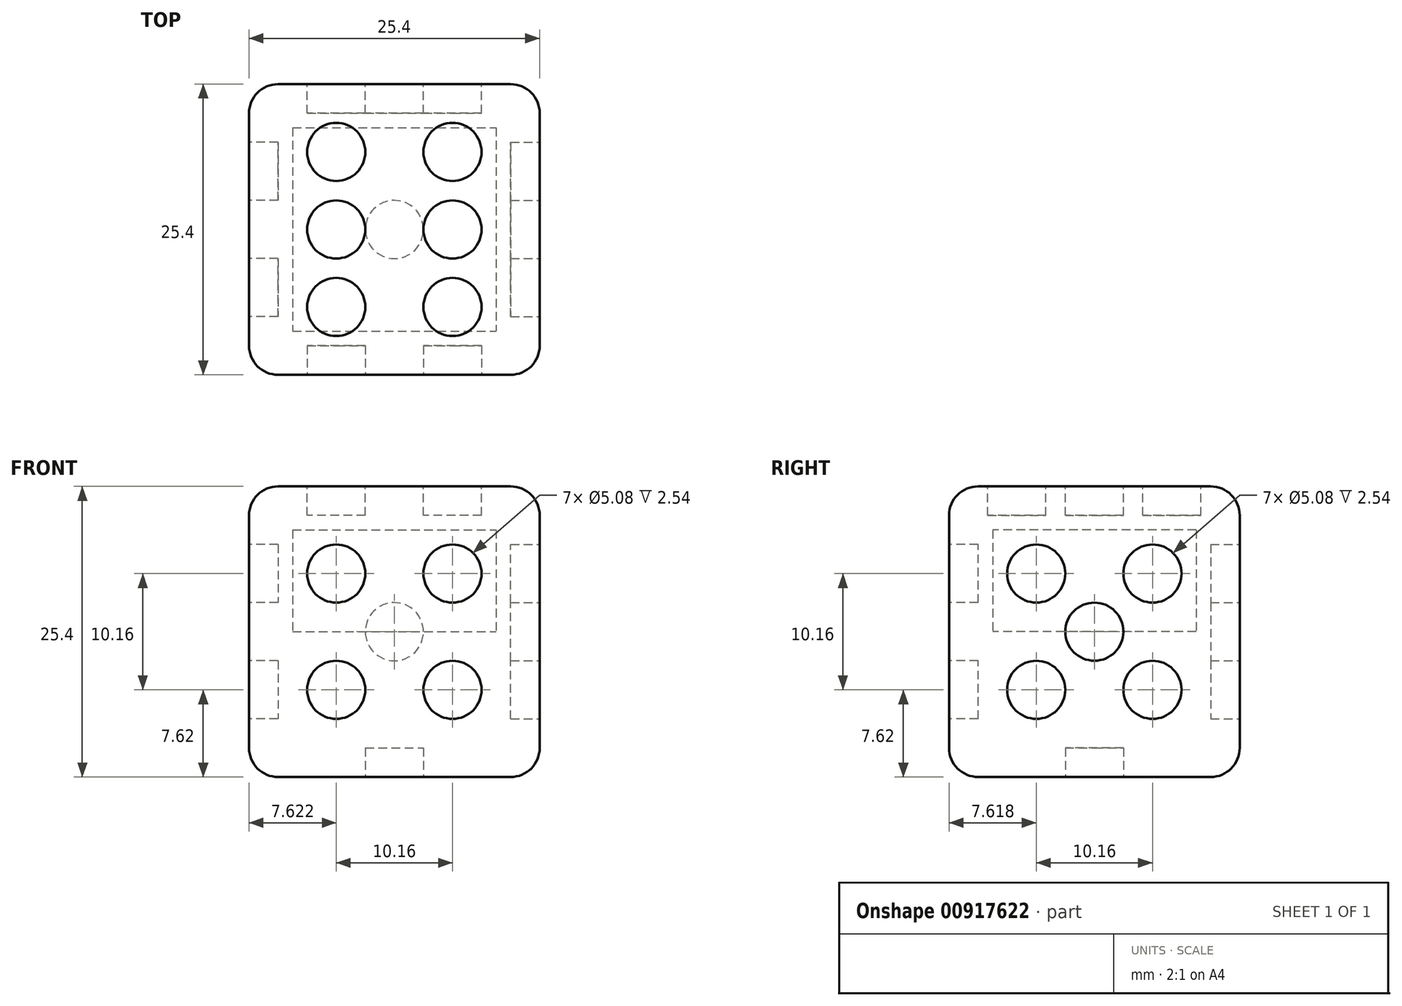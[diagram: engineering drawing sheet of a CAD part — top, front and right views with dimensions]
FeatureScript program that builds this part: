
annotation { "Feature Type Name" : "Feature", "Feature Type Description" : "" }
export const myFeature = defineFeature(function(context is Context, id is Id, definition is map)
    precondition{}
    {
        {
            var Q0;
            Q0=qCreatedBy(makeId("Top.planeOp"),FACE);
            var sketch = newSketch(context, id + "F0", { "sketchPlane" : qUnion([Q0])});
            skLineSegment(sketch, "E0.bottom", {"start": v(-52.85, 44.08) * mm, "end": v(-27.45, 44.08) * mm});
            skLineSegment(sketch, "E0.top", {"start": v(-52.85, 18.68) * mm, "end": v(-27.45, 18.68) * mm});
            skLineSegment(sketch, "E0.left", {"start": v(-52.85, 44.08) * mm, "end": v(-52.85, 18.68) * mm});
            skLineSegment(sketch, "E0.right", {"start": v(-27.45, 44.08) * mm, "end": v(-27.45, 18.68) * mm});
            skSolve(sketch);
        }
        {
            var Q0;
            Q0=makeQuery(id+"F0.imprint","IMPRINT",FACE,{"disambiguationData":[TD([[makeQuery(id+"F0.imprint","IMPRINT",EDGE,{"derivedFrom":sQuery(id+"F0.wireOp",EDGE,"E0.bottom")}),-1.0]])]});
            extrude(context, id + "F1", {"entities" : qUnion([Q0]), "depth" : 12.7 * mm, "offsetDistance" : 25.4 * mm});
        }
        {
            var Q0;
            Q0=makeQuery(id+"F1.opExtrude","CAP_FACE",FACE,{"disambiguationData":[OSD([sQuery(id+"F0.wireOp",EDGE,"E0.bottom"),sQuery(id+"F0.wireOp",EDGE,"E0.top"),sQuery(id+"F0.wireOp",EDGE,"E0.left"),sQuery(id+"F0.wireOp",EDGE,"E0.right")])],"isStart":false});
            var sketch = newSketch(context, id + "F2", { "sketchPlane" : qUnion([Q0])});
            skLineSegment(sketch, "E1.bottom", {"start": v(-49.04, 40.27) * mm, "end": v(-31.26, 40.27) * mm});
            skLineSegment(sketch, "E1.top", {"start": v(-49.04, 22.49) * mm, "end": v(-31.26, 22.49) * mm});
            skLineSegment(sketch, "E1.left", {"start": v(-49.04, 40.27) * mm, "end": v(-49.04, 22.49) * mm});
            skLineSegment(sketch, "E1.right", {"start": v(-31.26, 40.27) * mm, "end": v(-31.26, 22.49) * mm});
            skLineSegment(sketch, "E2.bottom", {"start": v(-52.85, 44.08) * mm, "end": v(-27.45, 44.08) * mm});
            skLineSegment(sketch, "E2.top", {"start": v(-52.85, 18.68) * mm, "end": v(-27.45, 18.68) * mm});
            skLineSegment(sketch, "E2.left", {"start": v(-52.85, 44.08) * mm, "end": v(-52.85, 18.68) * mm});
            skLineSegment(sketch, "E2.right", {"start": v(-27.45, 44.08) * mm, "end": v(-27.45, 18.68) * mm});
            skSolve(sketch);
        }
        {
            var Q0;
            Q0=makeQuery(id+"F2.imprint","IMPRINT",FACE,{"disambiguationData":[TD([[makeQuery(id+"F2.imprint","IMPRINT",EDGE,{"derivedFrom":sQuery(id+"F2.wireOp",EDGE,"E1.bottom")}),1.0]])]});
            extrude(context, id + "F3", {"entities" : qUnion([Q0]), "operationType" : NewBodyOperationType.ADD, "depth" : 8.9 * mm, "offsetDistance" : 25.4 * mm});
        }
        {
            var Q0;
            Q0=makeQuery(id+"F3.opExtrude","CAP_FACE",FACE,{"disambiguationData":[OSD([sQuery(id+"F2.wireOp",EDGE,"E1.bottom"),sQuery(id+"F2.wireOp",EDGE,"E1.top"),sQuery(id+"F2.wireOp",EDGE,"E1.left"),sQuery(id+"F2.wireOp",EDGE,"E1.right"),sQuery(id+"F2.wireOp",EDGE,"E2.bottom"),sQuery(id+"F2.wireOp",EDGE,"E2.top"),sQuery(id+"F2.wireOp",EDGE,"E2.left"),sQuery(id+"F2.wireOp",EDGE,"E2.right")])],"isStart":false});
            var sketch = newSketch(context, id + "F4", { "sketchPlane" : qUnion([Q0])});
            skLineSegment(sketch, "E3.bottom", {"start": v(-52.85, 44.08) * mm, "end": v(-27.45, 44.08) * mm});
            skLineSegment(sketch, "E3.top", {"start": v(-52.85, 18.68) * mm, "end": v(-27.45, 18.68) * mm});
            skLineSegment(sketch, "E3.left", {"start": v(-52.85, 44.08) * mm, "end": v(-52.85, 18.68) * mm});
            skLineSegment(sketch, "E3.right", {"start": v(-27.45, 44.08) * mm, "end": v(-27.45, 18.68) * mm});
            skSolve(sketch);
        }
        {
            var Q0;
            Q0 = qSketchRegion(id + "F4", true);
            extrude(context, id + "F5", {"entities" : qUnion([Q0]), "operationType" : NewBodyOperationType.ADD, "depth" : 3.8 * mm, "offsetDistance" : 25.4 * mm});
        }
        {
            var Q0;
            Q0=makeQuery(id+"F5.opExtrude","CAP_EDGE",EDGE,{"disambiguationData":[OSD([sQuery(id+"F4.wireOp",EDGE,"E3.top")])],"isStart":false});
            var Q1;
            Q1=makeQuery(id+"F5.opExtrude","CAP_EDGE",EDGE,{"disambiguationData":[OSD([sQuery(id+"F4.wireOp",EDGE,"E3.right")])],"isStart":false});
            var Q2;
            Q2=makeQuery(id+"F5.boolean.opBoolean","MERGE",EDGE,{"derivedFrom":[makeQuery(id+"F3.boolean.opBoolean","MERGE",EDGE,{"derivedFrom":[makeQuery(id+"F1.opExtrude","SWEPT_EDGE",EDGE,{"disambiguationData":[OSD([sQuery(id+"F0.wireOp",EDGE,"E0.top"),sQuery(id+"F0.wireOp",EDGE,"E0.right")])]}),makeQuery(id+"F3.opExtrude","SWEPT_EDGE",EDGE,{"disambiguationData":[OSD([sQuery(id+"F2.wireOp",EDGE,"E2.top"),sQuery(id+"F2.wireOp",EDGE,"E2.right")])]})]}),makeQuery(id+"F5.opExtrude","SWEPT_EDGE",EDGE,{"disambiguationData":[OSD([sQuery(id+"F4.wireOp",EDGE,"E3.top"),sQuery(id+"F4.wireOp",EDGE,"E3.right")])]})]});
            var Q3;
            Q3=makeQuery(id+"F5.boolean.opBoolean","MERGE",EDGE,{"derivedFrom":[makeQuery(id+"F3.boolean.opBoolean","MERGE",EDGE,{"derivedFrom":[makeQuery(id+"F1.opExtrude","SWEPT_EDGE",EDGE,{"disambiguationData":[OSD([sQuery(id+"F0.wireOp",EDGE,"E0.bottom"),sQuery(id+"F0.wireOp",EDGE,"E0.right")])]}),makeQuery(id+"F3.opExtrude","SWEPT_EDGE",EDGE,{"disambiguationData":[OSD([sQuery(id+"F2.wireOp",EDGE,"E2.bottom"),sQuery(id+"F2.wireOp",EDGE,"E2.right")])]})]}),makeQuery(id+"F5.opExtrude","SWEPT_EDGE",EDGE,{"disambiguationData":[OSD([sQuery(id+"F4.wireOp",EDGE,"E3.bottom"),sQuery(id+"F4.wireOp",EDGE,"E3.right")])]})]});
            var Q4;
            Q4=makeQuery(id+"F5.opExtrude","CAP_EDGE",EDGE,{"disambiguationData":[OSD([sQuery(id+"F4.wireOp",EDGE,"E3.bottom")])],"isStart":false});
            var Q5;
            Q5=makeQuery(id+"F5.opExtrude","CAP_EDGE",EDGE,{"disambiguationData":[OSD([sQuery(id+"F4.wireOp",EDGE,"E3.left")])],"isStart":false});
            var Q6;
            Q6=makeQuery(id+"F5.boolean.opBoolean","MERGE",EDGE,{"derivedFrom":[makeQuery(id+"F3.boolean.opBoolean","MERGE",EDGE,{"derivedFrom":[makeQuery(id+"F1.opExtrude","SWEPT_EDGE",EDGE,{"disambiguationData":[OSD([sQuery(id+"F0.wireOp",EDGE,"E0.top"),sQuery(id+"F0.wireOp",EDGE,"E0.left")])]}),makeQuery(id+"F3.opExtrude","SWEPT_EDGE",EDGE,{"disambiguationData":[OSD([sQuery(id+"F2.wireOp",EDGE,"E2.top"),sQuery(id+"F2.wireOp",EDGE,"E2.left")])]})]}),makeQuery(id+"F5.opExtrude","SWEPT_EDGE",EDGE,{"disambiguationData":[OSD([sQuery(id+"F4.wireOp",EDGE,"E3.top"),sQuery(id+"F4.wireOp",EDGE,"E3.left")])]})]});
            var Q7;
            Q7=makeQuery(id+"F1.opExtrude","CAP_EDGE",EDGE,{"disambiguationData":[OSD([sQuery(id+"F0.wireOp",EDGE,"E0.top")])],"isStart":true});
            var Q8;
            Q8=makeQuery(id+"F1.opExtrude","CAP_EDGE",EDGE,{"disambiguationData":[OSD([sQuery(id+"F0.wireOp",EDGE,"E0.left")])],"isStart":true});
            var Q9;
            Q9=makeQuery(id+"F1.opExtrude","CAP_EDGE",EDGE,{"disambiguationData":[OSD([sQuery(id+"F0.wireOp",EDGE,"E0.bottom")])],"isStart":true});
            var Q10;
            Q10=makeQuery(id+"F1.opExtrude","CAP_EDGE",EDGE,{"disambiguationData":[OSD([sQuery(id+"F0.wireOp",EDGE,"E0.right")])],"isStart":true});
            var Q11;
            Q11=makeQuery(id+"F5.boolean.opBoolean","MERGE",EDGE,{"derivedFrom":[makeQuery(id+"F3.boolean.opBoolean","MERGE",EDGE,{"derivedFrom":[makeQuery(id+"F1.opExtrude","SWEPT_EDGE",EDGE,{"disambiguationData":[OSD([sQuery(id+"F0.wireOp",EDGE,"E0.bottom"),sQuery(id+"F0.wireOp",EDGE,"E0.left")])]}),makeQuery(id+"F3.opExtrude","SWEPT_EDGE",EDGE,{"disambiguationData":[OSD([sQuery(id+"F2.wireOp",EDGE,"E2.bottom"),sQuery(id+"F2.wireOp",EDGE,"E2.left")])]})]}),makeQuery(id+"F5.opExtrude","SWEPT_EDGE",EDGE,{"disambiguationData":[OSD([sQuery(id+"F4.wireOp",EDGE,"E3.bottom"),sQuery(id+"F4.wireOp",EDGE,"E3.left")])]})]});
            fillet(context, id + "F6", {"entities" : qUnion([Q0, Q1, Q2, Q3, Q4, Q5, Q6, Q7, Q8, Q9, Q10, Q11]), "radius" : 2.54 * mm, "tangentPropagation" : true, "allowEdgeOverflow" : false});
        }
        {
            var Q0;
            Q0=makeQuery(id+"F5.opExtrude","CAP_FACE",FACE,{"disambiguationData":[OSD([sQuery(id+"F4.wireOp",EDGE,"E3.bottom"),sQuery(id+"F4.wireOp",EDGE,"E3.top"),sQuery(id+"F4.wireOp",EDGE,"E3.left"),sQuery(id+"F4.wireOp",EDGE,"E3.right")])],"isStart":false});
            var sketch = newSketch(context, id + "F7", { "sketchPlane" : qUnion([Q0])});
            skLineSegment(sketch, "E4", {"start": v(-50.3, 41.54) * mm, "end": v(-45.23, 41.54) * mm});
            skLineSegment(sketch, "E5", {"start": v(-29.99, 41.54) * mm, "end": v(-29.99, 38.15) * mm});
            skLineSegment(sketch, "E6", {"start": v(-29.99, 21.22) * mm, "end": v(-35.07, 21.22) * mm});
            skLineSegment(sketch, "E7", {"start": v(-50.3, 21.22) * mm, "end": v(-50.3, 24.6) * mm});
            skLineSegment(sketch, "E8", {"start": v(-50.3, 24.6) * mm, "end": v(-45.23, 24.6) * mm});
            skLineSegment(sketch, "E9", {"start": v(-45.23, 41.54) * mm, "end": v(-45.23, 38.15) * mm});
            skLineSegment(sketch, "E10", {"start": v(-29.99, 38.15) * mm, "end": v(-35.07, 38.15) * mm});
            skLineSegment(sketch, "E11", {"start": v(-35.07, 21.22) * mm, "end": v(-35.07, 24.6) * mm});
            skLineSegment(sketch, "E12", {"start": v(-45.23, 38.15) * mm, "end": v(-45.23, 31.38) * mm});
            skLineSegment(sketch, "E13", {"start": v(-35.07, 38.15) * mm, "end": v(-35.07, 31.38) * mm});
            skCircle(sketch, "E14", {"center": v(-45.23, 38.15) * mm, "radius": 2.54 * mm});
            skCircle(sketch, "E15", {"center": v(-45.23, 31.38) * mm, "radius": 2.54 * mm});
            skCircle(sketch, "E16", {"center": v(-45.23, 24.6) * mm, "radius": 2.54 * mm});
            skCircle(sketch, "E17", {"center": v(-35.07, 24.6) * mm, "radius": 2.54 * mm});
            skCircle(sketch, "E18", {"center": v(-35.07, 31.38) * mm, "radius": 2.54 * mm});
            skCircle(sketch, "E19", {"center": v(-35.07, 38.15) * mm, "radius": 2.54 * mm});
            skSolve(sketch);
        }
        {
            var Q0;
            {var subQ0=sQuery(id+"F7.wireOp",EDGE,"E12");var subQ1=sQuery(id+"F7.wireOp",EDGE,"E9");var subQ2=makeQuery(id+"F7.imprint","INTERSECT",VERTEX,{"derivedFrom":[subQ1,subQ0]});Q0=makeQuery(id+"F7.imprint","IMPRINT",FACE,{"disambiguationData":[TD([[makeQuery(id+"F7.imprint","IMPRINT",EDGE,{"disambiguationData":[TD([[subQ2,1.0]])],"derivedFrom":subQ1}),1.0]])]});}
            var Q1;
            {var subQ0=sQuery(id+"F7.wireOp",EDGE,"E12");var subQ1=sQuery(id+"F7.wireOp",EDGE,"E9");var subQ2=makeQuery(id+"F7.imprint","INTERSECT",VERTEX,{"derivedFrom":[subQ1,subQ0]});Q1=makeQuery(id+"F7.imprint","IMPRINT",FACE,{"disambiguationData":[TD([[makeQuery(id+"F7.imprint","IMPRINT",EDGE,{"disambiguationData":[TD([[subQ2,1.0]])],"derivedFrom":subQ1}),-1.0]])]});}
            var Q2;
            {var subQ0=sQuery(id+"F7.wireOp",EDGE,"E13");var subQ1=sQuery(id+"F7.wireOp",EDGE,"E10");var subQ2=makeQuery(id+"F7.imprint","INTERSECT",VERTEX,{"derivedFrom":[subQ1,subQ0]});Q2=makeQuery(id+"F7.imprint","IMPRINT",FACE,{"disambiguationData":[TD([[makeQuery(id+"F7.imprint","IMPRINT",EDGE,{"disambiguationData":[TD([[subQ2,1.0]])],"derivedFrom":subQ1}),-1.0]])]});}
            var Q3;
            {var subQ0=sQuery(id+"F7.wireOp",EDGE,"E13");var subQ1=sQuery(id+"F7.wireOp",EDGE,"E10");var subQ2=makeQuery(id+"F7.imprint","INTERSECT",VERTEX,{"derivedFrom":[subQ1,subQ0]});Q3=makeQuery(id+"F7.imprint","IMPRINT",FACE,{"disambiguationData":[TD([[makeQuery(id+"F7.imprint","IMPRINT",EDGE,{"disambiguationData":[TD([[subQ2,1.0]])],"derivedFrom":subQ1}),1.0]])]});}
            var Q4;
            Q4=makeQuery(id+"F7.imprint","IMPRINT",FACE,{"disambiguationData":[TD([[makeQuery(id+"F7.imprint","IMPRINT",EDGE,{"derivedFrom":sQuery(id+"F7.wireOp",EDGE,"E18")}),1.0]])]});
            var Q5;
            Q5=makeQuery(id+"F7.imprint","IMPRINT",FACE,{"disambiguationData":[TD([[makeQuery(id+"F7.imprint","IMPRINT",EDGE,{"derivedFrom":sQuery(id+"F7.wireOp",EDGE,"E17")}),1.0]])]});
            var Q6;
            Q6=makeQuery(id+"F7.imprint","IMPRINT",FACE,{"disambiguationData":[TD([[makeQuery(id+"F7.imprint","IMPRINT",EDGE,{"derivedFrom":sQuery(id+"F7.wireOp",EDGE,"E16")}),1.0]])]});
            var Q7;
            Q7=makeQuery(id+"F7.imprint","IMPRINT",FACE,{"disambiguationData":[TD([[makeQuery(id+"F7.imprint","IMPRINT",EDGE,{"derivedFrom":sQuery(id+"F7.wireOp",EDGE,"E15")}),1.0]])]});
            extrude(context, id + "F8", {"entities" : qUnion([Q0, Q1, Q2, Q3, Q4, Q5, Q6, Q7]), "operationType" : NewBodyOperationType.REMOVE, "oppositeDirection" : true, "depth" : 2.54 * mm, "offsetDistance" : 25.4 * mm});
        }
        {
            var Q0;
            Q0=makeQuery(id+"F5.boolean.opBoolean","MERGE",FACE,{"derivedFrom":[makeQuery(id+"F3.boolean.opBoolean","MERGE",FACE,{"derivedFrom":[makeQuery(id+"F1.opExtrude","SWEPT_FACE",FACE,{"disambiguationData":[OSD([sQuery(id+"F0.wireOp",EDGE,"E0.right")])]}),makeQuery(id+"F3.opExtrude","SWEPT_FACE",FACE,{"disambiguationData":[OSD([sQuery(id+"F2.wireOp",EDGE,"E2.right")])]})]}),makeQuery(id+"F5.opExtrude","SWEPT_FACE",FACE,{"disambiguationData":[OSD([sQuery(id+"F4.wireOp",EDGE,"E3.right")])]})]});
            var sketch = newSketch(context, id + "F9", { "sketchPlane" : qUnion([Q0])});
            skLineSegment(sketch, "E20", {"start": v(21.22, 22.86) * mm, "end": v(31.38, 22.86) * mm});
            skLineSegment(sketch, "E21", {"start": v(41.54, 22.86) * mm, "end": v(41.54, 12.7) * mm});
            skLineSegment(sketch, "E22", {"start": v(41.54, 12.7) * mm, "end": v(31.38, 12.7) * mm});
            skCircle(sketch, "E23", {"center": v(31.38, 12.7) * mm, "radius": 2.54 * mm});
            skLineSegment(sketch, "E24", {"start": v(21.22, 22.86) * mm, "end": v(26.3, 22.86) * mm});
            skLineSegment(sketch, "E25", {"start": v(26.3, 22.86) * mm, "end": v(26.3, 17.78) * mm});
            skCircle(sketch, "E26", {"center": v(26.3, 17.78) * mm, "radius": 2.54 * mm});
            skLineSegment(sketch, "E27", {"start": v(26.3, 17.78) * mm, "end": v(26.3, 7.62) * mm});
            skCircle(sketch, "E28", {"center": v(26.3, 7.62) * mm, "radius": 2.54 * mm});
            skLineSegment(sketch, "E29", {"start": v(41.54, 22.86) * mm, "end": v(41.54, 17.78) * mm});
            skLineSegment(sketch, "E30", {"start": v(41.54, 17.78) * mm, "end": v(36.46, 17.78) * mm});
            skCircle(sketch, "E31", {"center": v(36.46, 17.78) * mm, "radius": 2.54 * mm});
            skLineSegment(sketch, "E32", {"start": v(36.46, 17.78) * mm, "end": v(36.46, 7.62) * mm});
            skCircle(sketch, "E33", {"center": v(36.46, 7.62) * mm, "radius": 2.54 * mm});
            skSolve(sketch);
        }
        {
            var Q0;
            {var subQ0=sQuery(id+"F9.wireOp",EDGE,"E27");var subQ1=sQuery(id+"F9.wireOp",EDGE,"E25");var subQ2=makeQuery(id+"F9.imprint","INTERSECT",VERTEX,{"derivedFrom":[subQ1,subQ0]});Q0=makeQuery(id+"F9.imprint","IMPRINT",FACE,{"disambiguationData":[TD([[makeQuery(id+"F9.imprint","IMPRINT",EDGE,{"disambiguationData":[TD([[subQ2,1.0]])],"derivedFrom":subQ1}),1.0]])]});}
            var Q1;
            {var subQ0=sQuery(id+"F9.wireOp",EDGE,"E27");var subQ1=sQuery(id+"F9.wireOp",EDGE,"E25");var subQ2=makeQuery(id+"F9.imprint","INTERSECT",VERTEX,{"derivedFrom":[subQ1,subQ0]});Q1=makeQuery(id+"F9.imprint","IMPRINT",FACE,{"disambiguationData":[TD([[makeQuery(id+"F9.imprint","IMPRINT",EDGE,{"disambiguationData":[TD([[subQ2,1.0]])],"derivedFrom":subQ1}),-1.0]])]});}
            var Q2;
            Q2=makeQuery(id+"F9.imprint","IMPRINT",FACE,{"disambiguationData":[TD([[makeQuery(id+"F9.imprint","IMPRINT",EDGE,{"derivedFrom":sQuery(id+"F9.wireOp",EDGE,"E28")}),1.0]])]});
            var Q3;
            Q3=makeQuery(id+"F9.imprint","IMPRINT",FACE,{"disambiguationData":[TD([[makeQuery(id+"F9.imprint","IMPRINT",EDGE,{"derivedFrom":sQuery(id+"F9.wireOp",EDGE,"E23")}),1.0]])]});
            var Q4;
            {var subQ0=sQuery(id+"F9.wireOp",EDGE,"E32");var subQ1=sQuery(id+"F9.wireOp",EDGE,"E30");var subQ2=makeQuery(id+"F9.imprint","INTERSECT",VERTEX,{"derivedFrom":[subQ1,subQ0]});Q4=makeQuery(id+"F9.imprint","IMPRINT",FACE,{"disambiguationData":[TD([[makeQuery(id+"F9.imprint","IMPRINT",EDGE,{"disambiguationData":[TD([[subQ2,1.0]])],"derivedFrom":subQ1}),-1.0]])]});}
            var Q5;
            {var subQ0=sQuery(id+"F9.wireOp",EDGE,"E32");var subQ1=sQuery(id+"F9.wireOp",EDGE,"E30");var subQ2=makeQuery(id+"F9.imprint","INTERSECT",VERTEX,{"derivedFrom":[subQ1,subQ0]});Q5=makeQuery(id+"F9.imprint","IMPRINT",FACE,{"disambiguationData":[TD([[makeQuery(id+"F9.imprint","IMPRINT",EDGE,{"disambiguationData":[TD([[subQ2,1.0]])],"derivedFrom":subQ1}),1.0]])]});}
            var Q6;
            Q6=makeQuery(id+"F9.imprint","IMPRINT",FACE,{"disambiguationData":[TD([[makeQuery(id+"F9.imprint","IMPRINT",EDGE,{"derivedFrom":sQuery(id+"F9.wireOp",EDGE,"E33")}),1.0]])]});
            extrude(context, id + "F10", {"entities" : qUnion([Q0, Q1, Q2, Q3, Q4, Q5, Q6]), "operationType" : NewBodyOperationType.REMOVE, "oppositeDirection" : true, "depth" : 2.54 * mm, "offsetDistance" : 25.4 * mm});
        }
        {
            var Q0;
            Q0=makeQuery(id+"F5.boolean.opBoolean","MERGE",FACE,{"derivedFrom":[makeQuery(id+"F3.boolean.opBoolean","MERGE",FACE,{"derivedFrom":[makeQuery(id+"F1.opExtrude","SWEPT_FACE",FACE,{"disambiguationData":[OSD([sQuery(id+"F0.wireOp",EDGE,"E0.bottom")])]}),makeQuery(id+"F3.opExtrude","SWEPT_FACE",FACE,{"disambiguationData":[OSD([sQuery(id+"F2.wireOp",EDGE,"E2.bottom")])]})]}),makeQuery(id+"F5.opExtrude","SWEPT_FACE",FACE,{"disambiguationData":[OSD([sQuery(id+"F4.wireOp",EDGE,"E3.bottom")])]})]});
            var sketch = newSketch(context, id + "F11", { "sketchPlane" : qUnion([Q0])});
            skLineSegment(sketch, "E34", {"start": v(29.99, 22.86) * mm, "end": v(40.15, 22.86) * mm});
            skLineSegment(sketch, "E35", {"start": v(40.15, 22.86) * mm, "end": v(40.15, 12.7) * mm});
            skCircle(sketch, "E36", {"center": v(40.15, 12.7) * mm, "radius": 2.54 * mm});
            skLineSegment(sketch, "E37", {"start": v(29.99, 22.86) * mm, "end": v(35.07, 22.86) * mm});
            skLineSegment(sketch, "E38", {"start": v(35.07, 22.86) * mm, "end": v(35.07, 17.78) * mm});
            skLineSegment(sketch, "E39", {"start": v(50.3, 2.54) * mm, "end": v(45.23, 2.54) * mm});
            skLineSegment(sketch, "E40", {"start": v(45.23, 2.54) * mm, "end": v(45.23, 7.62) * mm});
            skCircle(sketch, "E41", {"center": v(35.07, 17.78) * mm, "radius": 2.54 * mm});
            skCircle(sketch, "E42", {"center": v(45.23, 7.62) * mm, "radius": 2.54 * mm});
            skSolve(sketch);
        }
        {
            var Q0;
            Q0=makeQuery(id+"F11.imprint","IMPRINT",FACE,{"disambiguationData":[TD([[makeQuery(id+"F11.imprint","IMPRINT",EDGE,{"derivedFrom":sQuery(id+"F11.wireOp",EDGE,"E41")}),1.0]])]});
            var Q1;
            Q1=makeQuery(id+"F11.imprint","IMPRINT",FACE,{"disambiguationData":[TD([[makeQuery(id+"F11.imprint","IMPRINT",EDGE,{"derivedFrom":sQuery(id+"F11.wireOp",EDGE,"E36")}),1.0]])]});
            var Q2;
            Q2=makeQuery(id+"F11.imprint","IMPRINT",FACE,{"disambiguationData":[TD([[makeQuery(id+"F11.imprint","IMPRINT",EDGE,{"derivedFrom":sQuery(id+"F11.wireOp",EDGE,"E42")}),1.0]])]});
            extrude(context, id + "F12", {"entities" : qUnion([Q0, Q1, Q2]), "operationType" : NewBodyOperationType.REMOVE, "oppositeDirection" : true, "depth" : 2.54 * mm, "offsetDistance" : 25.4 * mm});
        }
        {
            var Q0;
            Q0=makeQuery(id+"F5.boolean.opBoolean","MERGE",FACE,{"derivedFrom":[makeQuery(id+"F3.boolean.opBoolean","MERGE",FACE,{"derivedFrom":[makeQuery(id+"F1.opExtrude","SWEPT_FACE",FACE,{"disambiguationData":[OSD([sQuery(id+"F0.wireOp",EDGE,"E0.left")])]}),makeQuery(id+"F3.opExtrude","SWEPT_FACE",FACE,{"disambiguationData":[OSD([sQuery(id+"F2.wireOp",EDGE,"E2.left")])]})]}),makeQuery(id+"F5.opExtrude","SWEPT_FACE",FACE,{"disambiguationData":[OSD([sQuery(id+"F4.wireOp",EDGE,"E3.left")])]})]});
            var sketch = newSketch(context, id + "F13", { "sketchPlane" : qUnion([Q0])});
            skLineSegment(sketch, "E43", {"start": v(-41.54, 22.86) * mm, "end": v(-36.46, 22.86) * mm});
            skLineSegment(sketch, "E44", {"start": v(-36.46, 22.86) * mm, "end": v(-36.46, 17.78) * mm});
            skLineSegment(sketch, "E45", {"start": v(-21.22, 2.54) * mm, "end": v(-26.3, 2.54) * mm});
            skLineSegment(sketch, "E46", {"start": v(-26.3, 2.54) * mm, "end": v(-26.3, 7.62) * mm});
            skCircle(sketch, "E47", {"center": v(-36.46, 17.78) * mm, "radius": 2.54 * mm});
            skCircle(sketch, "E48", {"center": v(-26.3, 7.62) * mm, "radius": 2.54 * mm});
            skSolve(sketch);
        }
        {
            var Q0;
            Q0=makeQuery(id+"F13.imprint","IMPRINT",FACE,{"disambiguationData":[TD([[makeQuery(id+"F13.imprint","IMPRINT",EDGE,{"derivedFrom":sQuery(id+"F13.wireOp",EDGE,"E47")}),1.0]])]});
            var Q1;
            Q1=makeQuery(id+"F13.imprint","IMPRINT",FACE,{"disambiguationData":[TD([[makeQuery(id+"F13.imprint","IMPRINT",EDGE,{"derivedFrom":sQuery(id+"F13.wireOp",EDGE,"E48")}),1.0]])]});
            extrude(context, id + "F14", {"entities" : qUnion([Q0, Q1]), "operationType" : NewBodyOperationType.REMOVE, "oppositeDirection" : true, "depth" : 2.54 * mm, "offsetDistance" : 25.4 * mm});
        }
        {
            var Q0;
            Q0=makeQuery(id+"F5.boolean.opBoolean","MERGE",FACE,{"derivedFrom":[makeQuery(id+"F3.boolean.opBoolean","MERGE",FACE,{"derivedFrom":[makeQuery(id+"F1.opExtrude","SWEPT_FACE",FACE,{"disambiguationData":[OSD([sQuery(id+"F0.wireOp",EDGE,"E0.top")])]}),makeQuery(id+"F3.opExtrude","SWEPT_FACE",FACE,{"disambiguationData":[OSD([sQuery(id+"F2.wireOp",EDGE,"E2.top")])]})]}),makeQuery(id+"F5.opExtrude","SWEPT_FACE",FACE,{"disambiguationData":[OSD([sQuery(id+"F4.wireOp",EDGE,"E3.top")])]})]});
            var sketch = newSketch(context, id + "F15", { "sketchPlane" : qUnion([Q0])});
            skLineSegment(sketch, "E49", {"start": v(-50.3, 22.86) * mm, "end": v(-45.23, 22.86) * mm});
            skLineSegment(sketch, "E50", {"start": v(-45.23, 22.86) * mm, "end": v(-45.23, 17.78) * mm});
            skLineSegment(sketch, "E51", {"start": v(-29.99, 22.86) * mm, "end": v(-29.99, 17.78) * mm});
            skLineSegment(sketch, "E52", {"start": v(-29.99, 17.78) * mm, "end": v(-35.07, 17.78) * mm});
            skLineSegment(sketch, "E53", {"start": v(-29.99, 2.54) * mm, "end": v(-35.07, 2.54) * mm});
            skLineSegment(sketch, "E54", {"start": v(-35.07, 2.54) * mm, "end": v(-35.07, 7.62) * mm});
            skLineSegment(sketch, "E55", {"start": v(-50.3, 2.54) * mm, "end": v(-45.23, 2.54) * mm});
            skLineSegment(sketch, "E56", {"start": v(-45.23, 2.54) * mm, "end": v(-45.23, 7.62) * mm});
            skCircle(sketch, "E57", {"center": v(-45.23, 17.78) * mm, "radius": 2.54 * mm});
            skCircle(sketch, "E58", {"center": v(-35.07, 17.78) * mm, "radius": 2.54 * mm});
            skCircle(sketch, "E59", {"center": v(-35.07, 7.62) * mm, "radius": 2.54 * mm});
            skCircle(sketch, "E60", {"center": v(-45.23, 7.62) * mm, "radius": 2.54 * mm});
            skSolve(sketch);
        }
        {
            var Q0;
            Q0=makeQuery(id+"F15.imprint","IMPRINT",FACE,{"disambiguationData":[TD([[makeQuery(id+"F15.imprint","IMPRINT",EDGE,{"derivedFrom":sQuery(id+"F15.wireOp",EDGE,"E57")}),1.0]])]});
            var Q1;
            Q1=makeQuery(id+"F15.imprint","IMPRINT",FACE,{"disambiguationData":[TD([[makeQuery(id+"F15.imprint","IMPRINT",EDGE,{"derivedFrom":sQuery(id+"F15.wireOp",EDGE,"E58")}),1.0]])]});
            var Q2;
            Q2=makeQuery(id+"F15.imprint","IMPRINT",FACE,{"disambiguationData":[TD([[makeQuery(id+"F15.imprint","IMPRINT",EDGE,{"derivedFrom":sQuery(id+"F15.wireOp",EDGE,"E59")}),1.0]])]});
            var Q3;
            Q3=makeQuery(id+"F15.imprint","IMPRINT",FACE,{"disambiguationData":[TD([[makeQuery(id+"F15.imprint","IMPRINT",EDGE,{"derivedFrom":sQuery(id+"F15.wireOp",EDGE,"E60")}),1.0]])]});
            extrude(context, id + "F16", {"entities" : qUnion([Q0, Q1, Q2, Q3]), "operationType" : NewBodyOperationType.REMOVE, "oppositeDirection" : true, "depth" : 2.54 * mm, "offsetDistance" : 25.4 * mm});
        }
        {
            var Q0;
            Q0=makeQuery(id+"F1.opExtrude","CAP_FACE",FACE,{"disambiguationData":[OSD([sQuery(id+"F0.wireOp",EDGE,"E0.bottom"),sQuery(id+"F0.wireOp",EDGE,"E0.top"),sQuery(id+"F0.wireOp",EDGE,"E0.left"),sQuery(id+"F0.wireOp",EDGE,"E0.right")])],"isStart":true});
            var sketch = newSketch(context, id + "F17", { "sketchPlane" : qUnion([Q0])});
            skLineSegment(sketch, "E61", {"start": v(-50.3, -21.22) * mm, "end": v(-40.15, -21.22) * mm});
            skLineSegment(sketch, "E62", {"start": v(-29.99, -21.22) * mm, "end": v(-29.99, -31.38) * mm});
            skLineSegment(sketch, "E63", {"start": v(-40.15, -21.22) * mm, "end": v(-40.15, -31.38) * mm});
            skCircle(sketch, "E64", {"center": v(-40.15, -31.38) * mm, "radius": 2.54 * mm});
            skSolve(sketch);
        }
        {
            var Q0;
            Q0=makeQuery(id+"F17.imprint","IMPRINT",FACE,{"disambiguationData":[TD([[makeQuery(id+"F17.imprint","IMPRINT",EDGE,{"derivedFrom":sQuery(id+"F17.wireOp",EDGE,"E64")}),1.0]])]});
            extrude(context, id + "F18", {"entities" : qUnion([Q0]), "operationType" : NewBodyOperationType.REMOVE, "oppositeDirection" : true, "depth" : 2.54 * mm, "offsetDistance" : 25.4 * mm});
        }
        {
            var Q0;
            Q0=makeQuery(id+"F11.imprint","IMPRINT",FACE,{"disambiguationData":[TD([[makeQuery(id+"F11.imprint","IMPRINT",EDGE,{"derivedFrom":sQuery(id+"F11.wireOp",EDGE,"E41")}),1.0]])]});
            var Q1;
            Q1=makeQuery(id+"F11.imprint","IMPRINT",FACE,{"disambiguationData":[TD([[makeQuery(id+"F11.imprint","IMPRINT",EDGE,{"derivedFrom":sQuery(id+"F11.wireOp",EDGE,"E36")}),1.0]])]});
            var Q2;
            Q2=makeQuery(id+"F11.imprint","IMPRINT",FACE,{"disambiguationData":[TD([[makeQuery(id+"F11.imprint","IMPRINT",EDGE,{"derivedFrom":sQuery(id+"F11.wireOp",EDGE,"E42")}),1.0]])]});
            extrude(context, id + "F19", {"entities" : qUnion([Q0, Q1, Q2]), "oppositeDirection" : true, "depth" : 2.54 * mm, "offsetDistance" : 25.4 * mm});
        }
        {
            var Q0;
            {var subQ0=sQuery(id+"F9.wireOp",EDGE,"E27");var subQ1=sQuery(id+"F9.wireOp",EDGE,"E25");var subQ2=makeQuery(id+"F9.imprint","INTERSECT",VERTEX,{"derivedFrom":[subQ1,subQ0]});Q0=makeQuery(id+"F9.imprint","IMPRINT",FACE,{"disambiguationData":[TD([[makeQuery(id+"F9.imprint","IMPRINT",EDGE,{"disambiguationData":[TD([[subQ2,1.0]])],"derivedFrom":subQ1}),1.0]])]});}
            var Q1;
            {var subQ0=sQuery(id+"F9.wireOp",EDGE,"E27");var subQ1=sQuery(id+"F9.wireOp",EDGE,"E25");var subQ2=makeQuery(id+"F9.imprint","INTERSECT",VERTEX,{"derivedFrom":[subQ1,subQ0]});Q1=makeQuery(id+"F9.imprint","IMPRINT",FACE,{"disambiguationData":[TD([[makeQuery(id+"F9.imprint","IMPRINT",EDGE,{"disambiguationData":[TD([[subQ2,1.0]])],"derivedFrom":subQ1}),-1.0]])]});}
            var Q2;
            {var subQ0=sQuery(id+"F9.wireOp",EDGE,"E32");var subQ1=sQuery(id+"F9.wireOp",EDGE,"E30");var subQ2=makeQuery(id+"F9.imprint","INTERSECT",VERTEX,{"derivedFrom":[subQ1,subQ0]});Q2=makeQuery(id+"F9.imprint","IMPRINT",FACE,{"disambiguationData":[TD([[makeQuery(id+"F9.imprint","IMPRINT",EDGE,{"disambiguationData":[TD([[subQ2,1.0]])],"derivedFrom":subQ1}),-1.0]])]});}
            var Q3;
            {var subQ0=sQuery(id+"F9.wireOp",EDGE,"E32");var subQ1=sQuery(id+"F9.wireOp",EDGE,"E30");var subQ2=makeQuery(id+"F9.imprint","INTERSECT",VERTEX,{"derivedFrom":[subQ1,subQ0]});Q3=makeQuery(id+"F9.imprint","IMPRINT",FACE,{"disambiguationData":[TD([[makeQuery(id+"F9.imprint","IMPRINT",EDGE,{"disambiguationData":[TD([[subQ2,1.0]])],"derivedFrom":subQ1}),1.0]])]});}
            var Q4;
            Q4=makeQuery(id+"F9.imprint","IMPRINT",FACE,{"disambiguationData":[TD([[makeQuery(id+"F9.imprint","IMPRINT",EDGE,{"derivedFrom":sQuery(id+"F9.wireOp",EDGE,"E28")}),1.0]])]});
            var Q5;
            Q5=makeQuery(id+"F9.imprint","IMPRINT",FACE,{"disambiguationData":[TD([[makeQuery(id+"F9.imprint","IMPRINT",EDGE,{"derivedFrom":sQuery(id+"F9.wireOp",EDGE,"E23")}),1.0]])]});
            var Q6;
            Q6=makeQuery(id+"F9.imprint","IMPRINT",FACE,{"disambiguationData":[TD([[makeQuery(id+"F9.imprint","IMPRINT",EDGE,{"derivedFrom":sQuery(id+"F9.wireOp",EDGE,"E33")}),1.0]])]});
            extrude(context, id + "F20", {"entities" : qUnion([Q0, Q1, Q2, Q3, Q4, Q5, Q6]), "oppositeDirection" : true, "depth" : 2.54 * mm, "offsetDistance" : 25.4 * mm});
        }
        {
            var Q0;
            Q0=makeQuery(id+"F13.imprint","IMPRINT",FACE,{"disambiguationData":[TD([[makeQuery(id+"F13.imprint","IMPRINT",EDGE,{"derivedFrom":sQuery(id+"F13.wireOp",EDGE,"E47")}),1.0]])]});
            var Q1;
            Q1=makeQuery(id+"F13.imprint","IMPRINT",FACE,{"disambiguationData":[TD([[makeQuery(id+"F13.imprint","IMPRINT",EDGE,{"derivedFrom":sQuery(id+"F13.wireOp",EDGE,"E48")}),1.0]])]});
            extrude(context, id + "F21", {"entities" : qUnion([Q0, Q1]), "oppositeDirection" : true, "depth" : 2.54 * mm, "offsetDistance" : 25.4 * mm});
        }
        {
            var Q0;
            Q0=makeQuery(id+"F15.imprint","IMPRINT",FACE,{"disambiguationData":[TD([[makeQuery(id+"F15.imprint","IMPRINT",EDGE,{"derivedFrom":sQuery(id+"F15.wireOp",EDGE,"E57")}),1.0]])]});
            var Q1;
            Q1=makeQuery(id+"F15.imprint","IMPRINT",FACE,{"disambiguationData":[TD([[makeQuery(id+"F15.imprint","IMPRINT",EDGE,{"derivedFrom":sQuery(id+"F15.wireOp",EDGE,"E58")}),1.0]])]});
            var Q2;
            Q2=makeQuery(id+"F15.imprint","IMPRINT",FACE,{"disambiguationData":[TD([[makeQuery(id+"F15.imprint","IMPRINT",EDGE,{"derivedFrom":sQuery(id+"F15.wireOp",EDGE,"E59")}),1.0]])]});
            var Q3;
            Q3=makeQuery(id+"F15.imprint","IMPRINT",FACE,{"disambiguationData":[TD([[makeQuery(id+"F15.imprint","IMPRINT",EDGE,{"derivedFrom":sQuery(id+"F15.wireOp",EDGE,"E60")}),1.0]])]});
            extrude(context, id + "F22", {"entities" : qUnion([Q0, Q1, Q2, Q3]), "oppositeDirection" : true, "depth" : 2.54 * mm, "offsetDistance" : 25.4 * mm});
        }
        {
            var Q0;
            Q0=makeQuery(id+"F17.imprint","IMPRINT",FACE,{"disambiguationData":[TD([[makeQuery(id+"F17.imprint","IMPRINT",EDGE,{"derivedFrom":sQuery(id+"F17.wireOp",EDGE,"E64")}),1.0]])]});
            extrude(context, id + "F23", {"entities" : qUnion([Q0]), "oppositeDirection" : true, "depth" : 2.54 * mm, "offsetDistance" : 25.4 * mm});
        }
        {
            var Q0;
            {var subQ0=sQuery(id+"F7.wireOp",EDGE,"E12");var subQ1=sQuery(id+"F7.wireOp",EDGE,"E9");var subQ2=makeQuery(id+"F7.imprint","INTERSECT",VERTEX,{"derivedFrom":[subQ1,subQ0]});Q0=makeQuery(id+"F7.imprint","IMPRINT",FACE,{"disambiguationData":[TD([[makeQuery(id+"F7.imprint","IMPRINT",EDGE,{"disambiguationData":[TD([[subQ2,1.0]])],"derivedFrom":subQ1}),-1.0]])]});}
            var Q1;
            {var subQ0=sQuery(id+"F7.wireOp",EDGE,"E12");var subQ1=sQuery(id+"F7.wireOp",EDGE,"E9");var subQ2=makeQuery(id+"F7.imprint","INTERSECT",VERTEX,{"derivedFrom":[subQ1,subQ0]});Q1=makeQuery(id+"F7.imprint","IMPRINT",FACE,{"disambiguationData":[TD([[makeQuery(id+"F7.imprint","IMPRINT",EDGE,{"disambiguationData":[TD([[subQ2,1.0]])],"derivedFrom":subQ1}),1.0]])]});}
            var Q2;
            Q2=makeQuery(id+"F7.imprint","IMPRINT",FACE,{"disambiguationData":[TD([[makeQuery(id+"F7.imprint","IMPRINT",EDGE,{"derivedFrom":sQuery(id+"F7.wireOp",EDGE,"E15")}),1.0]])]});
            var Q3;
            Q3=makeQuery(id+"F7.imprint","IMPRINT",FACE,{"disambiguationData":[TD([[makeQuery(id+"F7.imprint","IMPRINT",EDGE,{"derivedFrom":sQuery(id+"F7.wireOp",EDGE,"E16")}),1.0]])]});
            var Q4;
            Q4=makeQuery(id+"F7.imprint","IMPRINT",FACE,{"disambiguationData":[TD([[makeQuery(id+"F7.imprint","IMPRINT",EDGE,{"derivedFrom":sQuery(id+"F7.wireOp",EDGE,"E17")}),1.0]])]});
            var Q5;
            Q5=makeQuery(id+"F7.imprint","IMPRINT",FACE,{"disambiguationData":[TD([[makeQuery(id+"F7.imprint","IMPRINT",EDGE,{"derivedFrom":sQuery(id+"F7.wireOp",EDGE,"E18")}),1.0]])]});
            var Q6;
            {var subQ0=sQuery(id+"F7.wireOp",EDGE,"E13");var subQ1=sQuery(id+"F7.wireOp",EDGE,"E10");var subQ2=makeQuery(id+"F7.imprint","INTERSECT",VERTEX,{"derivedFrom":[subQ1,subQ0]});Q6=makeQuery(id+"F7.imprint","IMPRINT",FACE,{"disambiguationData":[TD([[makeQuery(id+"F7.imprint","IMPRINT",EDGE,{"disambiguationData":[TD([[subQ2,1.0]])],"derivedFrom":subQ1}),-1.0]])]});}
            var Q7;
            {var subQ0=sQuery(id+"F7.wireOp",EDGE,"E13");var subQ1=sQuery(id+"F7.wireOp",EDGE,"E10");var subQ2=makeQuery(id+"F7.imprint","INTERSECT",VERTEX,{"derivedFrom":[subQ1,subQ0]});Q7=makeQuery(id+"F7.imprint","IMPRINT",FACE,{"disambiguationData":[TD([[makeQuery(id+"F7.imprint","IMPRINT",EDGE,{"disambiguationData":[TD([[subQ2,1.0]])],"derivedFrom":subQ1}),1.0]])]});}
            extrude(context, id + "F24", {"entities" : qUnion([Q0, Q1, Q2, Q3, Q4, Q5, Q6, Q7]), "oppositeDirection" : true, "depth" : 2.54 * mm, "offsetDistance" : 25.4 * mm});
        }
    });
